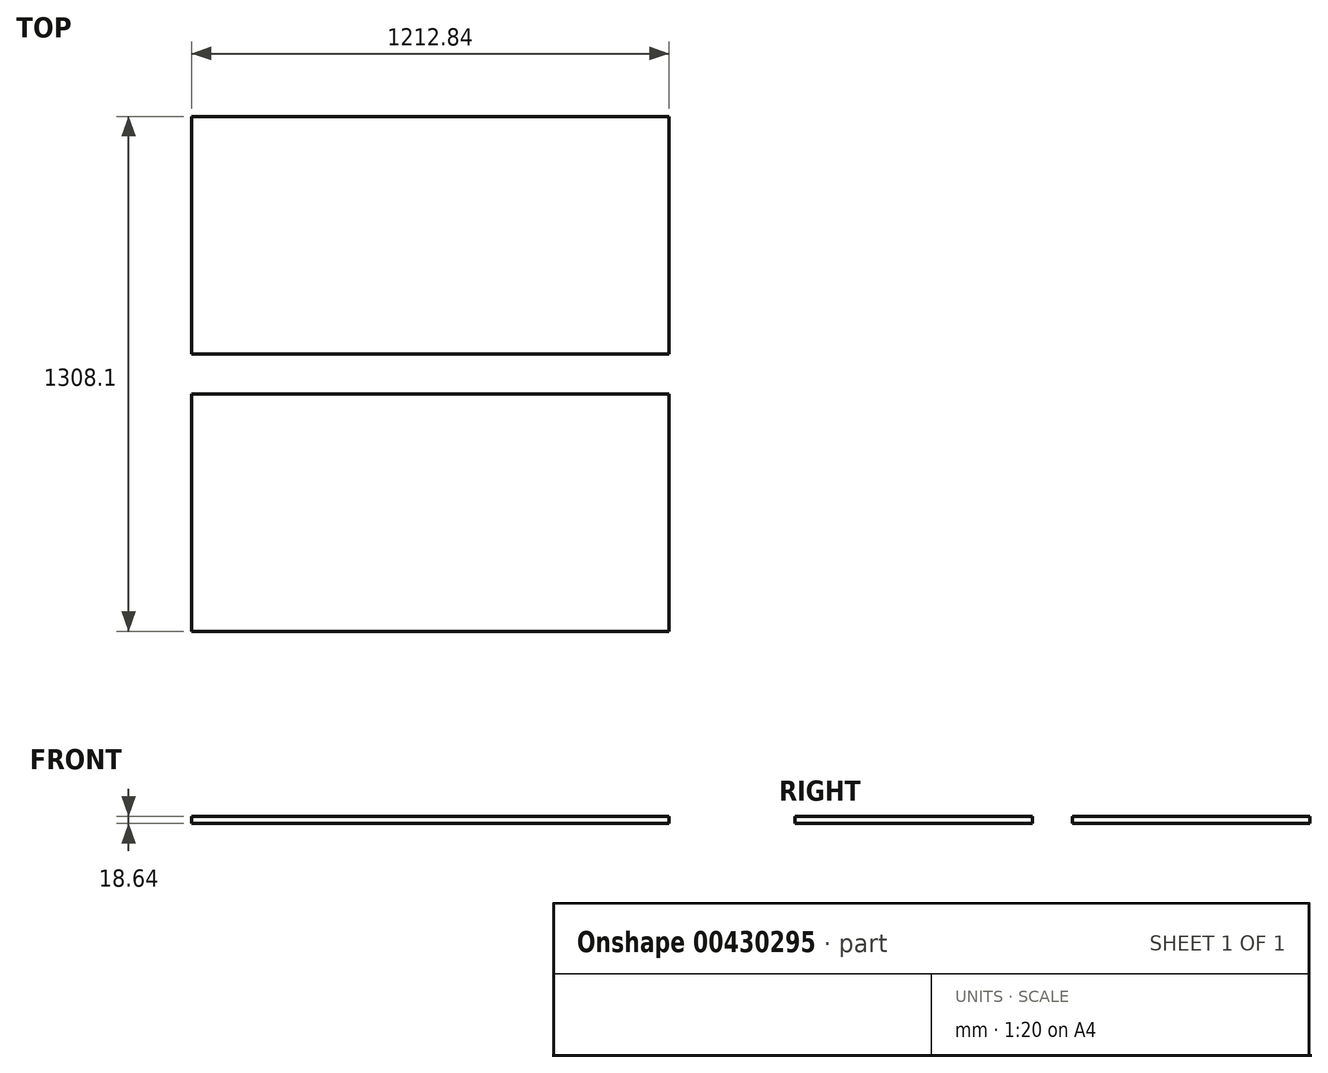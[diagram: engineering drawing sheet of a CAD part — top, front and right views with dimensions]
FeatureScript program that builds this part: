
annotation { "Feature Type Name" : "Feature", "Feature Type Description" : "" }
export const myFeature = defineFeature(function(context is Context, id is Id, definition is map)
    precondition{}
    {
        {
            var Q0;
            Q0=qCreatedBy(makeId("Top.planeOp"),FACE);
            var sketch = newSketch(context, id + "F0", { "sketchPlane" : qUnion([Q0])});
            skLineSegment(sketch, "E0.bottom", {"start": v(606.43, 301.62) * mm, "end": v(-606.43, 301.62) * mm});
            skLineSegment(sketch, "E0.top", {"start": v(606.43, -301.63) * mm, "end": v(-606.43, -301.63) * mm});
            skLineSegment(sketch, "E0.left", {"start": v(606.43, 301.62) * mm, "end": v(606.43, -301.63) * mm});
            skLineSegment(sketch, "E0.right", {"start": v(-606.43, 301.62) * mm, "end": v(-606.43, -301.63) * mm});
            skPoint(sketch, "E0.middle", {"position": v(0, 0) * mm});
            skLineSegment(sketch, "E1.bottom", {"start": v(-606.43, -403.23) * mm, "end": v(606.43, -403.23) * mm});
            skLineSegment(sketch, "E1.top", {"start": v(-606.43, -1006.48) * mm, "end": v(606.43, -1006.48) * mm});
            skLineSegment(sketch, "E1.left", {"start": v(-606.43, -403.23) * mm, "end": v(-606.43, -1006.48) * mm});
            skLineSegment(sketch, "E1.right", {"start": v(606.43, -403.23) * mm, "end": v(606.43, -1006.48) * mm});
            skLineSegment(sketch, "E2", {"start": v(-606.43, -301.63) * mm, "end": v(-606.43, -403.23) * mm, "construction": true});
            skSolve(sketch);
        }
        {
            var Q0;
            Q0=makeQuery(id+"F0.imprint","IMPRINT",FACE,{"disambiguationData":[TD([[makeQuery(id+"F0.imprint","IMPRINT",EDGE,{"derivedFrom":sQuery(id+"F0.wireOp",EDGE,"E0.bottom")}),1.0]])]});
            var Q1;
            Q1=makeQuery(id+"F0.imprint","IMPRINT",FACE,{"disambiguationData":[TD([[makeQuery(id+"F0.imprint","IMPRINT",EDGE,{"derivedFrom":sQuery(id+"F0.wireOp",EDGE,"E1.bottom")}),-1.0]])]});
            extrude(context, id + "F1", {"entities" : qUnion([Q0, Q1]), "depth" : 18.64 * mm, "offsetDistance" : 25.4 * mm});
        }
        {
            var Q0;
            Q0=makeQuery(id+"F1.opExtrude","CAP_FACE",FACE,{"disambiguationData":[OSD([sQuery(id+"F0.wireOp",EDGE,"E0.bottom"),sQuery(id+"F0.wireOp",EDGE,"E0.top"),sQuery(id+"F0.wireOp",EDGE,"E0.left"),sQuery(id+"F0.wireOp",EDGE,"E0.right")])],"isStart":false});
            var sketch = newSketch(context, id + "F2", { "sketchPlane" : qUnion([Q0])});
            skLineSegment(sketch, "E3", {"start": v(606.43, 198.28) * mm, "end": v(606.43, -301.63) * mm});
            skLineSegment(sketch, "E4.MirrorCS", {"start": v(412.3, 282.89) * mm, "end": v(377.34, 207.94) * mm});
            skLineSegment(sketch, "E5.MirrorCS", {"start": v(144.15, 294.4) * mm, "end": v(144.15, -169.55) * mm, "construction": true});
            skLineSegment(sketch, "E6.MirrorCS", {"start": v(417.66, 294.4) * mm, "end": v(144.15, 294.4) * mm, "construction": true});
            skLineSegment(sketch, "E7.MirrorCS", {"start": v(599.1, 209.8) * mm, "end": v(429.17, 289.03) * mm});
            skLineSegment(sketch, "E8", {"start": v(606.43, -301.63) * mm, "end": v(144.15, -301.63) * mm});
            skLineSegment(sketch, "E9", {"start": v(144.15, -301.63) * mm, "end": v(144.15, -180.2) * mm});
            skLineSegment(sketch, "E10", {"start": v(374.72, 202.32) * mm, "end": v(374.72, 294.4) * mm, "construction": true});
            skLineSegment(sketch, "E11", {"start": v(154.64, -167.7) * mm, "end": v(267.13, -147.86) * mm});
            skArc(sketch, "E12", {"start": v(271.12, -146.44) * mm, "mid": v(393, 3.96) * mm, "end": v(377.48, 196.92) * mm});
            skPoint(sketch, "E13.visualSharp", {"position": v(144.15, -169.55) * mm});
            skArc(sketch, "E13.filletArc", {"start": v(154.64, -167.7) * mm, "mid": v(147.12, -172.04) * mm, "end": v(144.15, -180.2) * mm});
            skPoint(sketch, "E14.visualSharp", {"position": v(269.22, -147.5) * mm});
            skArc(sketch, "E14.filletArc", {"start": v(267.13, -147.86) * mm, "mid": v(269.18, -147.32) * mm, "end": v(271.12, -146.44) * mm});
            skPoint(sketch, "E15.visualSharp", {"position": v(374.72, 202.32) * mm});
            skArc(sketch, "E15.filletArc", {"start": v(377.34, 207.94) * mm, "mid": v(376.15, 202.42) * mm, "end": v(377.48, 196.92) * mm});
            skPoint(sketch, "E16.visualSharp", {"position": v(417.66, 294.4) * mm});
            skArc(sketch, "E16.filletArc", {"start": v(429.17, 289.03) * mm, "mid": v(419.46, 289.45) * mm, "end": v(412.3, 282.89) * mm});
            skPoint(sketch, "E17.visualSharp", {"position": v(606.42, 206.38) * mm});
            skArc(sketch, "E17.filletArc", {"start": v(606.43, 198.28) * mm, "mid": v(604.44, 205.1) * mm, "end": v(599.1, 209.8) * mm});
            skSolve(sketch);
        }
        {
            var Q0;
            Q0 = qConstructionFilter(qBodyType(qCreatedBy(id + "F2" ,EDGE), BodyType.WIRE), ConstructionObject.NO);
            extrude(context, id + "F3", {"bodyType" : ToolBodyType.SURFACE, "surfaceEntities" : qUnion([Q0]), "depth" : 0.25 * mm, "offsetDistance" : 25.4 * mm});
        }
        {
            var Q0;
            Q0=makeQuery(id+"F1.opExtrude","CAP_FACE",FACE,{"disambiguationData":[OSD([sQuery(id+"F0.wireOp",EDGE,"E0.bottom"),sQuery(id+"F0.wireOp",EDGE,"E0.top"),sQuery(id+"F0.wireOp",EDGE,"E0.left"),sQuery(id+"F0.wireOp",EDGE,"E0.right")])],"isStart":false});
            var sketch = newSketch(context, id + "F4", { "sketchPlane" : qUnion([Q0])});
            skLineSegment(sketch, "E18", {"start": v(-109.85, -198.28) * mm, "end": v(-109.85, 301.62) * mm});
            skLineSegment(sketch, "E19.MirrorCS", {"start": v(84.28, -282.89) * mm, "end": v(119.23, -207.94) * mm});
            skLineSegment(sketch, "E20.MirrorCS", {"start": v(352.43, -294.4) * mm, "end": v(352.43, 169.54) * mm, "construction": true});
            skLineSegment(sketch, "E21.MirrorCS", {"start": v(78.91, -294.4) * mm, "end": v(352.43, -294.4) * mm, "construction": true});
            skLineSegment(sketch, "E22.MirrorCS", {"start": v(-102.52, -209.8) * mm, "end": v(67.4, -289.03) * mm});
            skLineSegment(sketch, "E23", {"start": v(-109.85, 301.62) * mm, "end": v(352.43, 301.62) * mm});
            skLineSegment(sketch, "E24", {"start": v(352.43, 301.62) * mm, "end": v(352.43, 180.2) * mm});
            skLineSegment(sketch, "E25", {"start": v(121.85, -202.32) * mm, "end": v(121.85, -294.4) * mm, "construction": true});
            skLineSegment(sketch, "E26", {"start": v(341.93, 167.7) * mm, "end": v(229.44, 147.86) * mm});
            skArc(sketch, "E27", {"start": v(225.45, 146.44) * mm, "mid": v(103.57, -3.96) * mm, "end": v(119.1, -196.92) * mm});
            skPoint(sketch, "E28.visualSharp", {"position": v(352.43, 169.54) * mm});
            skArc(sketch, "E28.filletArc", {"start": v(341.93, 167.7) * mm, "mid": v(349.45, 172.04) * mm, "end": v(352.43, 180.2) * mm});
            skPoint(sketch, "E29.visualSharp", {"position": v(227.35, 147.5) * mm});
            skArc(sketch, "E29.filletArc", {"start": v(229.44, 147.86) * mm, "mid": v(227.39, 147.32) * mm, "end": v(225.45, 146.44) * mm});
            skPoint(sketch, "E30.visualSharp", {"position": v(121.85, -202.32) * mm});
            skArc(sketch, "E30.filletArc", {"start": v(119.23, -207.94) * mm, "mid": v(120.42, -202.42) * mm, "end": v(119.1, -196.92) * mm});
            skPoint(sketch, "E31.visualSharp", {"position": v(78.91, -294.4) * mm});
            skArc(sketch, "E31.filletArc", {"start": v(67.4, -289.03) * mm, "mid": v(77.11, -289.45) * mm, "end": v(84.28, -282.89) * mm});
            skPoint(sketch, "E32.visualSharp", {"position": v(-109.85, -206.38) * mm});
            skArc(sketch, "E32.filletArc", {"start": v(-109.85, -198.28) * mm, "mid": v(-107.87, -205.1) * mm, "end": v(-102.52, -209.8) * mm});
            skSolve(sketch);
        }
        {
            var Q0;
            Q0=makeQuery(id+"F4.imprint","IMPRINT",FACE,{"disambiguationData":[TD([[makeQuery(id+"F4.imprint","IMPRINT",EDGE,{"derivedFrom":sQuery(id+"F4.wireOp",EDGE,"E18")}),-1.0]])]});
            var Q1;
            Q1 = qConstructionFilter(qBodyType(qCreatedBy(id + "F4" ,EDGE), BodyType.WIRE), ConstructionObject.NO);
            extrude(context, id + "F5", {"entities" : qUnion([Q0]), "bodyType" : ToolBodyType.SURFACE, "operationType" : NewBodyOperationType.ADD, "surfaceEntities" : qUnion([Q1]), "depth" : 0.03 * mm, "offsetDistance" : 25.4 * mm});
        }
        {
            var Q0;
            Q0=makeQuery(id+"F1.opExtrude","CAP_FACE",FACE,{"disambiguationData":[OSD([sQuery(id+"F0.wireOp",EDGE,"E1.bottom"),sQuery(id+"F0.wireOp",EDGE,"E1.top"),sQuery(id+"F0.wireOp",EDGE,"E1.left"),sQuery(id+"F0.wireOp",EDGE,"E1.right")])],"isStart":false});
            var sketch = newSketch(context, id + "F6", { "sketchPlane" : qUnion([Q0])});
            skLineSegment(sketch, "E33", {"start": v(-120.01, -1006.48) * mm, "end": v(-606.43, -536.58) * mm, "construction": true});
            skLineSegment(sketch, "E34.bottom", {"start": v(-528.32, -949.33) * mm, "end": v(-198.12, -949.33) * mm});
            skLineSegment(sketch, "E34.top", {"start": v(-528.32, -593.73) * mm, "end": v(-198.12, -593.73) * mm});
            skLineSegment(sketch, "E34.left", {"start": v(-541.02, -936.62) * mm, "end": v(-541.02, -606.43) * mm});
            skLineSegment(sketch, "E34.right", {"start": v(-185.42, -936.62) * mm, "end": v(-185.42, -606.43) * mm});
            skPoint(sketch, "E34.middle", {"position": v(-363.22, -771.52) * mm});
            skPoint(sketch, "E35.visualSharp", {"position": v(-541.02, -593.73) * mm});
            skArc(sketch, "E35.filletArc", {"start": v(-528.32, -593.73) * mm, "mid": v(-537.3, -597.44) * mm, "end": v(-541.02, -606.43) * mm});
            skPoint(sketch, "E36.visualSharp", {"position": v(-185.42, -593.73) * mm});
            skArc(sketch, "E36.filletArc", {"start": v(-185.42, -606.43) * mm, "mid": v(-189.14, -597.44) * mm, "end": v(-198.12, -593.73) * mm});
            skPoint(sketch, "E37.visualSharp", {"position": v(-541.02, -949.33) * mm});
            skArc(sketch, "E37.filletArc", {"start": v(-541.02, -936.62) * mm, "mid": v(-537.3, -945.6) * mm, "end": v(-528.32, -949.32) * mm});
            skPoint(sketch, "E38.visualSharp", {"position": v(-185.42, -949.33) * mm});
            skArc(sketch, "E38.filletArc", {"start": v(-198.12, -949.33) * mm, "mid": v(-189.14, -945.6) * mm, "end": v(-185.42, -936.62) * mm});
            skArc(sketch, "E39.0", {"start": v(-198.12, -952.5) * mm, "mid": v(-186.9, -947.85) * mm, "end": v(-182.24, -936.62) * mm});
            skLineSegment(sketch, "E39.1", {"start": v(-528.32, -952.5) * mm, "end": v(-198.12, -952.5) * mm});
            skLineSegment(sketch, "E39.2", {"start": v(-182.25, -936.62) * mm, "end": v(-182.25, -606.43) * mm});
            skArc(sketch, "E39.3", {"start": v(-544.2, -936.62) * mm, "mid": v(-539.55, -947.85) * mm, "end": v(-528.32, -952.5) * mm});
            skArc(sketch, "E39.4", {"start": v(-182.25, -606.43) * mm, "mid": v(-186.9, -595.2) * mm, "end": v(-198.12, -590.55) * mm});
            skLineSegment(sketch, "E39.5", {"start": v(-528.32, -590.55) * mm, "end": v(-198.12, -590.55) * mm});
            skArc(sketch, "E39.6", {"start": v(-528.32, -590.55) * mm, "mid": v(-539.55, -595.2) * mm, "end": v(-544.2, -606.43) * mm});
            skLineSegment(sketch, "E39.7", {"start": v(-544.2, -936.62) * mm, "end": v(-544.2, -606.43) * mm});
            skLineSegment(sketch, "E40.bottom", {"start": v(-606.42, -536.57) * mm, "end": v(-120.02, -536.57) * mm});
            skLineSegment(sketch, "E40.top", {"start": v(-606.42, -1006.48) * mm, "end": v(-120.02, -1006.48) * mm});
            skLineSegment(sketch, "E40.left", {"start": v(-606.43, -536.57) * mm, "end": v(-606.43, -1006.48) * mm});
            skLineSegment(sketch, "E40.right", {"start": v(-120.02, -536.57) * mm, "end": v(-120.02, -1006.48) * mm});
            skSolve(sketch);
        }
        {
            var Q0;
            Q0=makeQuery(id+"F6.imprint","IMPRINT",FACE,{"disambiguationData":[TD([[makeQuery(id+"F6.imprint","IMPRINT",EDGE,{"derivedFrom":sQuery(id+"F6.wireOp",EDGE,"E39.0")}),-1.0]])]});
            var Q1;
            Q1=makeQuery(id+"F6.imprint","IMPRINT",FACE,{"disambiguationData":[TD([[makeQuery(id+"F6.imprint","IMPRINT",EDGE,{"derivedFrom":sQuery(id+"F6.wireOp",EDGE,"E34.bottom")}),1.0]])]});
            var Q2;
            Q2 = qConstructionFilter(qBodyType(qCreatedBy(id + "F6" ,EDGE), BodyType.WIRE), ConstructionObject.NO);
            extrude(context, id + "F7", {"entities" : qUnion([Q0, Q1]), "bodyType" : ToolBodyType.SURFACE, "surfaceEntities" : qUnion([Q2]), "depth" : 0.03 * mm, "offsetDistance" : 25.4 * mm});
        }
        {
            var Q0;
            Q0=makeQuery(id+"F1.opExtrude","CAP_FACE",FACE,{"disambiguationData":[OSD([sQuery(id+"F0.wireOp",EDGE,"E1.bottom"),sQuery(id+"F0.wireOp",EDGE,"E1.top"),sQuery(id+"F0.wireOp",EDGE,"E1.left"),sQuery(id+"F0.wireOp",EDGE,"E1.right")])],"isStart":false});
            var sketch = newSketch(context, id + "F8", { "sketchPlane" : qUnion([Q0])});
            skLineSegment(sketch, "E41.bottom", {"start": v(318.13, -1006.48) * mm, "end": v(-107.32, -1006.48) * mm});
            skLineSegment(sketch, "E41.top", {"start": v(318.13, -536.58) * mm, "end": v(-107.32, -536.58) * mm});
            skLineSegment(sketch, "E41.left", {"start": v(318.13, -1006.48) * mm, "end": v(318.13, -536.58) * mm});
            skLineSegment(sketch, "E41.right", {"start": v(-107.32, -1006.48) * mm, "end": v(-107.32, -536.58) * mm});
            skSolve(sketch);
        }
        {
            var Q0;
            Q0 = qSketchRegion(id + "F8", true);
            var Q1;
            Q1 = qConstructionFilter(qBodyType(qCreatedBy(id + "F8" ,EDGE), BodyType.WIRE), ConstructionObject.NO);
            extrude(context, id + "F9", {"entities" : qUnion([Q0]), "bodyType" : ToolBodyType.SURFACE, "surfaceEntities" : qUnion([Q1]), "depth" : 0.03 * mm, "offsetDistance" : 25.4 * mm});
        }
        {
            var Q0;
            Q0=makeQuery(id+"F1.opExtrude","CAP_FACE",FACE,{"disambiguationData":[OSD([sQuery(id+"F0.wireOp",EDGE,"E1.bottom"),sQuery(id+"F0.wireOp",EDGE,"E1.top"),sQuery(id+"F0.wireOp",EDGE,"E1.left"),sQuery(id+"F0.wireOp",EDGE,"E1.right")])],"isStart":false});
            var sketch = newSketch(context, id + "F10", { "sketchPlane" : qUnion([Q0])});
            skLineSegment(sketch, "E42.bottom", {"start": v(-136.53, -520.07) * mm, "end": v(-606.43, -520.07) * mm});
            skLineSegment(sketch, "E42.top", {"start": v(-136.53, -403.23) * mm, "end": v(-606.43, -403.23) * mm});
            skLineSegment(sketch, "E42.left", {"start": v(-136.53, -520.07) * mm, "end": v(-136.53, -403.23) * mm});
            skLineSegment(sketch, "E42.right", {"start": v(-606.43, -520.07) * mm, "end": v(-606.43, -403.23) * mm});
            skSolve(sketch);
        }
        {
            var Q0;
            Q0 = qSketchRegion(id + "F10", true);
            var Q1;
            Q1=sQuery(id+"F10.wireOp",EDGE,"E42.top");
            var Q2;
            Q2=sQuery(id+"F10.wireOp",EDGE,"E42.left");
            var Q3;
            Q3=sQuery(id+"F10.wireOp",EDGE,"E42.bottom");
            var Q4;
            Q4=sQuery(id+"F10.wireOp",EDGE,"E42.right");
            extrude(context, id + "F11", {"entities" : qUnion([Q0]), "bodyType" : ToolBodyType.SURFACE, "surfaceEntities" : qUnion([Q1, Q2, Q3, Q4]), "depth" : 0.03 * mm, "offsetDistance" : 25.4 * mm});
        }
        {
            var Q0;
            Q0=makeQuery(id+"F1.opExtrude","CAP_FACE",FACE,{"disambiguationData":[OSD([sQuery(id+"F0.wireOp",EDGE,"E1.bottom"),sQuery(id+"F0.wireOp",EDGE,"E1.top"),sQuery(id+"F0.wireOp",EDGE,"E1.left"),sQuery(id+"F0.wireOp",EDGE,"E1.right")])],"isStart":false});
            var sketch = newSketch(context, id + "F12", { "sketchPlane" : qUnion([Q0])});
            skLineSegment(sketch, "E43.bottom", {"start": v(606.43, -504.83) * mm, "end": v(136.53, -504.83) * mm});
            skLineSegment(sketch, "E43.top", {"start": v(606.43, -403.23) * mm, "end": v(136.53, -403.23) * mm});
            skLineSegment(sketch, "E43.left", {"start": v(606.43, -504.83) * mm, "end": v(606.43, -403.23) * mm});
            skLineSegment(sketch, "E43.right", {"start": v(136.52, -504.83) * mm, "end": v(136.52, -403.23) * mm});
            skSolve(sketch);
        }
        {
            var Q0;
            Q0=makeQuery(id+"F12.imprint","IMPRINT",FACE,{"disambiguationData":[TD([[makeQuery(id+"F12.imprint","IMPRINT",EDGE,{"derivedFrom":sQuery(id+"F12.wireOp",EDGE,"E43.bottom")}),1.0]])]});
            var Q1;
            Q1=sQuery(id+"F12.wireOp",EDGE,"E43.right");
            var Q2;
            Q2=sQuery(id+"F12.wireOp",EDGE,"E43.top");
            var Q3;
            Q3=sQuery(id+"F12.wireOp",EDGE,"E43.left");
            var Q4;
            Q4=sQuery(id+"F12.wireOp",EDGE,"E43.bottom");
            extrude(context, id + "F13", {"entities" : qUnion([Q0]), "bodyType" : ToolBodyType.SURFACE, "surfaceEntities" : qUnion([Q1, Q2, Q3, Q4]), "depth" : 0.03 * mm, "offsetDistance" : 25.4 * mm});
        }
        {
            var Q0;
            Q0=makeQuery(id+"F1.opExtrude","CAP_FACE",FACE,{"disambiguationData":[OSD([sQuery(id+"F0.wireOp",EDGE,"E0.bottom"),sQuery(id+"F0.wireOp",EDGE,"E0.top"),sQuery(id+"F0.wireOp",EDGE,"E0.left"),sQuery(id+"F0.wireOp",EDGE,"E0.right")])],"isStart":false});
            var sketch = newSketch(context, id + "F14", { "sketchPlane" : qUnion([Q0])});
            skLineSegment(sketch, "E44.bottom", {"start": v(-606.43, 301.62) * mm, "end": v(-136.53, 301.62) * mm});
            skLineSegment(sketch, "E44.top", {"start": v(-606.43, -102.74) * mm, "end": v(-136.53, -102.74) * mm});
            skLineSegment(sketch, "E44.left", {"start": v(-606.43, 301.62) * mm, "end": v(-606.43, -102.74) * mm});
            skLineSegment(sketch, "E44.right", {"start": v(-136.53, 301.62) * mm, "end": v(-136.53, -102.74) * mm});
            skLineSegment(sketch, "E45.left", {"start": v(-606.43, -102.74) * mm, "end": v(-606.43, -102.74) * mm});
            skLineSegment(sketch, "E45.right", {"start": v(-136.53, -102.74) * mm, "end": v(-136.53, -102.74) * mm});
            skSolve(sketch);
        }
        {
            var Q0;
            Q0 = qSketchRegion(id + "F14", true);
            var Q1;
            Q1=sQuery(id+"F14.wireOp",EDGE,"E44.left");
            var Q2;
            Q2=sQuery(id+"F14.wireOp",EDGE,"E44.bottom");
            var Q3;
            Q3=sQuery(id+"F14.wireOp",EDGE,"E44.right");
            var Q4;
            Q4=sQuery(id+"F14.wireOp",EDGE,"E44.top");
            extrude(context, id + "F15", {"entities" : qUnion([Q0]), "bodyType" : ToolBodyType.SURFACE, "operationType" : NewBodyOperationType.ADD, "surfaceEntities" : qUnion([Q1, Q2, Q3, Q4]), "oppositeDirection" : true, "depth" : 0.03 * mm, "offsetDistance" : 25.4 * mm});
        }
        {
            var Q0;
            Q0=makeQuery(id+"F1.opExtrude","CAP_FACE",FACE,{"disambiguationData":[OSD([sQuery(id+"F0.wireOp",EDGE,"E0.bottom"),sQuery(id+"F0.wireOp",EDGE,"E0.top"),sQuery(id+"F0.wireOp",EDGE,"E0.left"),sQuery(id+"F0.wireOp",EDGE,"E0.right")])],"isStart":false});
            var sketch = newSketch(context, id + "F16", { "sketchPlane" : qUnion([Q0])});
            skLineSegment(sketch, "E46.bottom", {"start": v(-606.43, -102.74) * mm, "end": v(-136.53, -102.74) * mm});
            skLineSegment(sketch, "E46.top", {"start": v(-606.43, -301.63) * mm, "end": v(-136.53, -301.63) * mm});
            skLineSegment(sketch, "E46.left", {"start": v(-606.43, -102.74) * mm, "end": v(-606.43, -301.63) * mm});
            skLineSegment(sketch, "E46.right", {"start": v(-136.53, -102.74) * mm, "end": v(-136.53, -301.63) * mm});
            skSolve(sketch);
        }
        {
            var Q0;
            Q0=sQuery(id+"F16.wireOp",EDGE,"E46.left");
            var Q1;
            Q1=sQuery(id+"F16.wireOp",EDGE,"E46.bottom");
            var Q2;
            Q2=sQuery(id+"F16.wireOp",EDGE,"E46.right");
            var Q3;
            Q3=sQuery(id+"F16.wireOp",EDGE,"E46.top");
            extrude(context, id + "F17", {"bodyType" : ToolBodyType.SURFACE, "surfaceEntities" : qUnion([Q0, Q1, Q2, Q3]), "depth" : 0.03 * mm, "offsetDistance" : 25.4 * mm});
        }
        {
            var Q0;
            Q0=makeQuery(id+"F1.opExtrude","CAP_FACE",FACE,{"disambiguationData":[OSD([sQuery(id+"F0.wireOp",EDGE,"E1.bottom"),sQuery(id+"F0.wireOp",EDGE,"E1.top"),sQuery(id+"F0.wireOp",EDGE,"E1.left"),sQuery(id+"F0.wireOp",EDGE,"E1.right")])],"isStart":false});
            var sketch = newSketch(context, id + "F18", { "sketchPlane" : qUnion([Q0])});
            skLineSegment(sketch, "E47.bottom", {"start": v(400.69, -1006.48) * mm, "end": v(606.43, -1006.48) * mm});
            skLineSegment(sketch, "E47.top", {"start": v(400.69, -536.58) * mm, "end": v(606.43, -536.58) * mm});
            skLineSegment(sketch, "E47.left", {"start": v(400.69, -1006.48) * mm, "end": v(400.69, -536.58) * mm});
            skLineSegment(sketch, "E47.right", {"start": v(606.42, -1006.48) * mm, "end": v(606.42, -536.58) * mm});
            skSolve(sketch);
        }
        {
            var Q0;
            Q0=sQuery(id+"F18.wireOp",EDGE,"E47.left");
            var Q1;
            Q1=sQuery(id+"F18.wireOp",EDGE,"E47.top");
            var Q2;
            Q2=sQuery(id+"F18.wireOp",EDGE,"E47.right");
            var Q3;
            Q3=sQuery(id+"F18.wireOp",EDGE,"E47.bottom");
            extrude(context, id + "F19", {"bodyType" : ToolBodyType.SURFACE, "surfaceEntities" : qUnion([Q0, Q1, Q2, Q3]), "depth" : 0.03 * mm, "offsetDistance" : 25.4 * mm});
        }
        {
            var Q0;
            Q0=makeQuery(id+"F1.opExtrude","CAP_FACE",FACE,{"disambiguationData":[OSD([sQuery(id+"F0.wireOp",EDGE,"E0.bottom"),sQuery(id+"F0.wireOp",EDGE,"E0.top"),sQuery(id+"F0.wireOp",EDGE,"E0.left"),sQuery(id+"F0.wireOp",EDGE,"E0.right")])],"isStart":false});
            var sketch = newSketch(context, id + "F20", { "sketchPlane" : qUnion([Q0])});
            skLineSegment(sketch, "E48.bottom", {"start": v(-201.3, -67.82) * mm, "end": v(-541.66, -67.82) * mm});
            skLineSegment(sketch, "E48.top", {"start": v(-201.3, 205.23) * mm, "end": v(-541.66, 205.23) * mm});
            skLineSegment(sketch, "E48.left", {"start": v(-201.3, -67.82) * mm, "end": v(-201.3, 205.23) * mm});
            skLineSegment(sketch, "E48.right", {"start": v(-541.66, -67.82) * mm, "end": v(-541.66, 205.23) * mm});
            skPoint(sketch, "E48.middle", {"position": v(-371.48, 68.7) * mm});
            skLineSegment(sketch, "E49", {"start": v(-371.48, 68.7) * mm, "end": v(-371.48, -102.74) * mm, "construction": true});
            skSolve(sketch);
        }
        {
            var Q0;
            Q0=sQuery(id+"F20.wireOp",EDGE,"E48.right");
            var Q1;
            Q1=sQuery(id+"F20.wireOp",EDGE,"E48.top");
            var Q2;
            Q2=sQuery(id+"F20.wireOp",EDGE,"E48.left");
            var Q3;
            Q3=sQuery(id+"F20.wireOp",EDGE,"E48.bottom");
            extrude(context, id + "F21", {"bodyType" : ToolBodyType.SURFACE, "surfaceEntities" : qUnion([Q0, Q1, Q2, Q3]), "depth" : 0.03 * mm, "offsetDistance" : 25.4 * mm});
        }
    });
